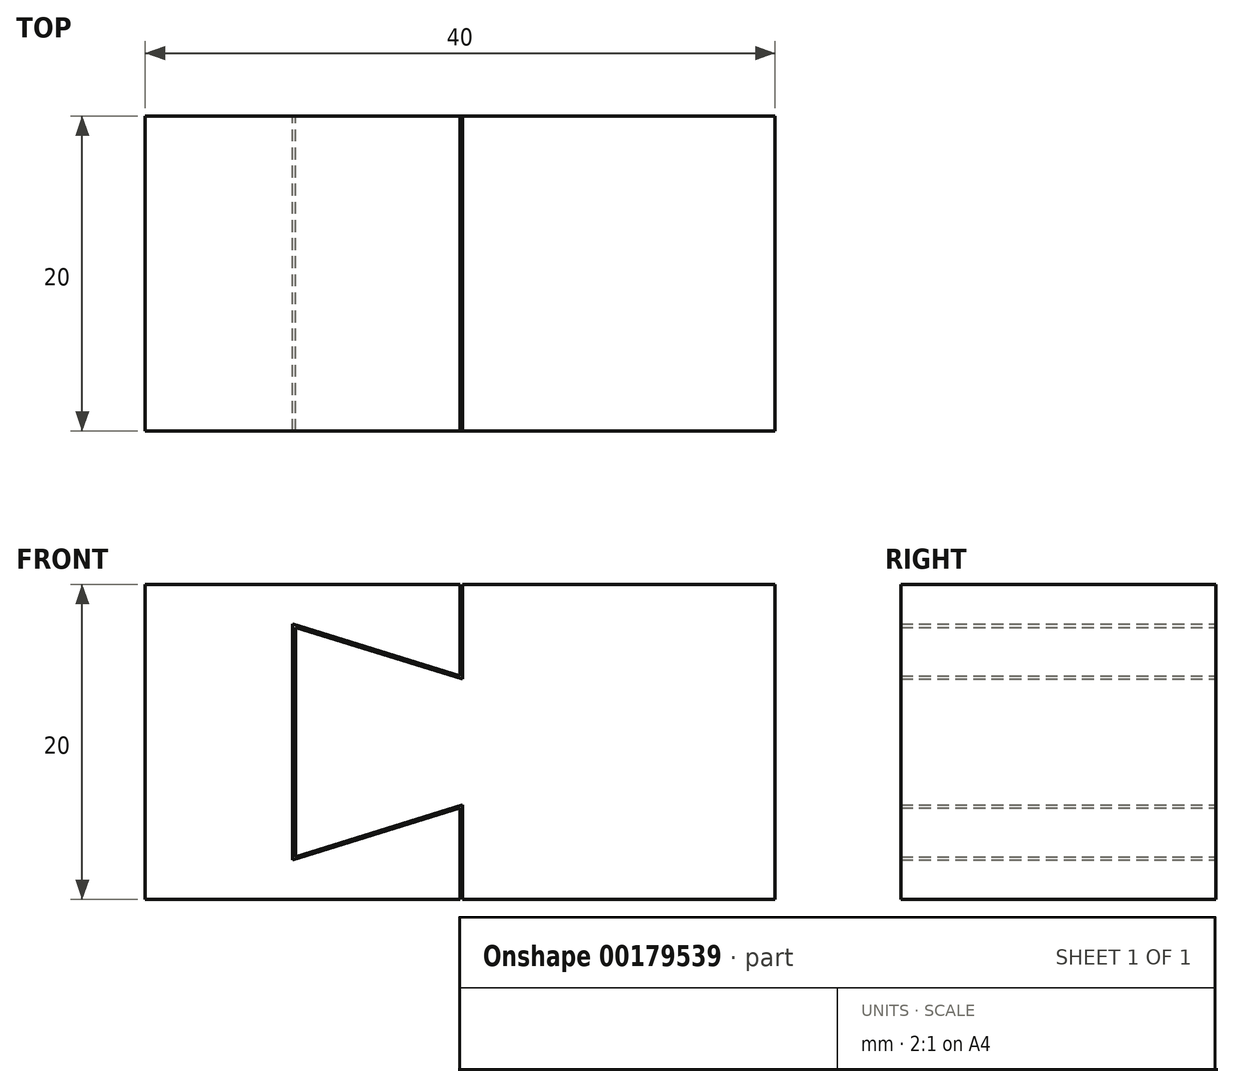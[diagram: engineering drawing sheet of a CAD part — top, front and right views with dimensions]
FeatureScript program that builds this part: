
annotation { "Feature Type Name" : "Feature", "Feature Type Description" : "" }
export const myFeature = defineFeature(function(context is Context, id is Id, definition is map)
    precondition{}
    {
        {
            var Q0;
            Q0=qCreatedBy(makeId("Top.planeOp"),FACE);
            var sketch = newSketch(context, id + "F0", { "sketchPlane" : qUnion([Q0])});
            skLineSegment(sketch, "E0.bottom", {"start": v(-20, 10) * mm, "end": v(20, 10) * mm});
            skLineSegment(sketch, "E0.top", {"start": v(-20, -10) * mm, "end": v(20, -10) * mm});
            skLineSegment(sketch, "E0.left", {"start": v(-20, 10) * mm, "end": v(-20, -10) * mm});
            skLineSegment(sketch, "E0.right", {"start": v(20, 10) * mm, "end": v(20, -10) * mm});
            skSolve(sketch);
        }
        {
            var Q0;
            Q0=makeQuery(id+"F0.imprint","IMPRINT",FACE,{"disambiguationData":[TD([[makeQuery(id+"F0.imprint","IMPRINT",EDGE,{"derivedFrom":sQuery(id+"F0.wireOp",EDGE,"E0.bottom")}),-1.0]])]});
            extrude(context, id + "F1", {"entities" : qUnion([Q0]), "depth" : 20 * mm});
        }
        {
            var Q0;
            Q0=makeQuery(id+"F1.opExtrude","SWEPT_FACE",FACE,{"disambiguationData":[OSD([sQuery(id+"F0.wireOp",EDGE,"E0.bottom")])]});
            var sketch = newSketch(context, id + "F2", { "sketchPlane" : qUnion([Q0])});
            skLineSegment(sketch, "E1", {"start": v(0, 0) * mm, "end": v(0, 5.8) * mm});
            skLineSegment(sketch, "E2", {"start": v(0, 5.8) * mm, "end": v(10.64, 2.5) * mm});
            skLineSegment(sketch, "E3", {"start": v(10.64, 2.5) * mm, "end": v(10.64, 17.5) * mm});
            skLineSegment(sketch, "E4", {"start": v(10.64, 17.5) * mm, "end": v(0, 14.2) * mm});
            skLineSegment(sketch, "E5", {"start": v(0, 14.2) * mm, "end": v(0, 20) * mm});
            skLineSegment(sketch, "E6", {"start": v(0, 20) * mm, "end": v(-0.15, 20) * mm});
            skLineSegment(sketch, "E7", {"start": v(-0.15, 20) * mm, "end": v(-0.15, 14) * mm});
            skLineSegment(sketch, "E8", {"start": v(-0.15, 14) * mm, "end": v(10.46, 17.29) * mm});
            skLineSegment(sketch, "E9", {"start": v(10.46, 17.29) * mm, "end": v(10.46, 2.71) * mm});
            skLineSegment(sketch, "E10", {"start": v(10.46, 2.71) * mm, "end": v(-0.15, 6) * mm});
            skLineSegment(sketch, "E11", {"start": v(-0.15, 6) * mm, "end": v(-0.15, 0) * mm});
            skLineSegment(sketch, "E12", {"start": v(-0.15, 0) * mm, "end": v(0, 0) * mm});
            skSolve(sketch);
        }
        {
            var Q0;
            Q0=makeQuery(id+"F2.imprint","IMPRINT",FACE,{"disambiguationData":[TD([[makeQuery(id+"F2.imprint","IMPRINT",EDGE,{"derivedFrom":sQuery(id+"F2.wireOp",EDGE,"E1")}),1.0]])]});
            extrude(context, id + "F3", {"entities" : qUnion([Q0]), "operationType" : NewBodyOperationType.REMOVE, "oppositeDirection" : true, "depth" : 25 * mm});
        }
    });
